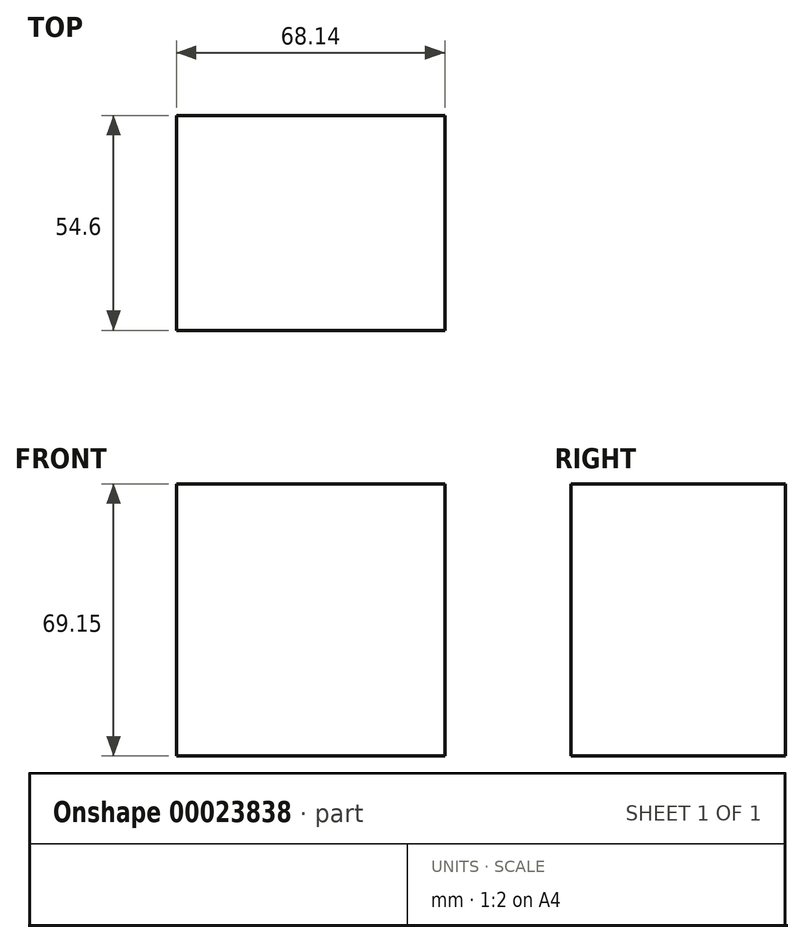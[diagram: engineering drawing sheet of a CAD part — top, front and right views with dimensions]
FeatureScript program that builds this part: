
annotation { "Feature Type Name" : "Feature", "Feature Type Description" : "" }
export const myFeature = defineFeature(function(context is Context, id is Id, definition is map)
    precondition{}
    {
        {
            var Q0;
            Q0=qCreatedBy(makeId("Front.planeOp"),FACE);
            var sketch = newSketch(context, id + "F0", { "sketchPlane" : qUnion([Q0])});
            skLineSegment(sketch, "E0.bottom", {"start": v(-33.94, 33.88) * mm, "end": v(34.2, 33.88) * mm});
            skLineSegment(sketch, "E0.top", {"start": v(-33.94, -35.27) * mm, "end": v(34.2, -35.27) * mm});
            skLineSegment(sketch, "E0.left", {"start": v(-33.94, 33.88) * mm, "end": v(-33.94, -35.27) * mm});
            skLineSegment(sketch, "E0.right", {"start": v(34.2, 33.88) * mm, "end": v(34.2, -35.27) * mm});
            skSolve(sketch);
        }
        {
            var Q0;
            Q0=makeQuery(id+"F0.imprint","IMPRINT",FACE,{"disambiguationData":[TD([[makeQuery(id+"F0.imprint","IMPRINT",EDGE,{"derivedFrom":sQuery(id+"F0.wireOp",EDGE,"E0.bottom")}),-1.0]])]});
            extrude(context, id + "F1", {"entities" : qUnion([Q0]), "depth" : 54.6 * mm});
        }
    });
